# Revit family: Haworth_Belong_ToolRail_SurfaceMount
name_source: partatom
category: Furniture Systems
revit_build: Autodesk Revit 2018 (Build: 20170223_1515(x64)
units: mm (PartAtom-declared; Revit-internal decimal feet)

## family parameters
Always vertical = Yes
Cut with Voids When Loaded = No
OmniClass Number = 23.40.70.14.64.21
OmniClass Title = Systems Furniture
Part Type = Normal
Room Calculation Point = No
Round Connector Dimension = Use Diameter
Shared = No
Work Plane-Based = No

## types (1)
- Belong Tool Rail
    Actual Depth = 1 1/4"
    Actual Height = 28"
    Actual Width = 42"
    Assembly Code = E2020200
    Bracket Spacing = 30"
    Center Post = No
    Custom Size = No
    Description = Haworth - Belong Tools - Rail
    Frame Finish = Haworth _ Paint _ Gray Tone
    Manufacturer = Haworth
    Max. Width = 96"
    Min. Width = 24"
    Min/Max Width = 24-96 in. in 6 in. increments
    Model = Haworth - Belong Tools - Rail
    Revision Number = 3
    Size = Verify Final Dim. w/ Haworth
    Sustainability Info = https://www.haworth.com
    URL = www.haworth.com
    URL - Product = http://www.haworth.com
    Warranty = http://www.haworth.com
    Width = 42"

## geometry (parser evidence)
native form markers: Sweep x3
no freeform markers — native parametric forms only
